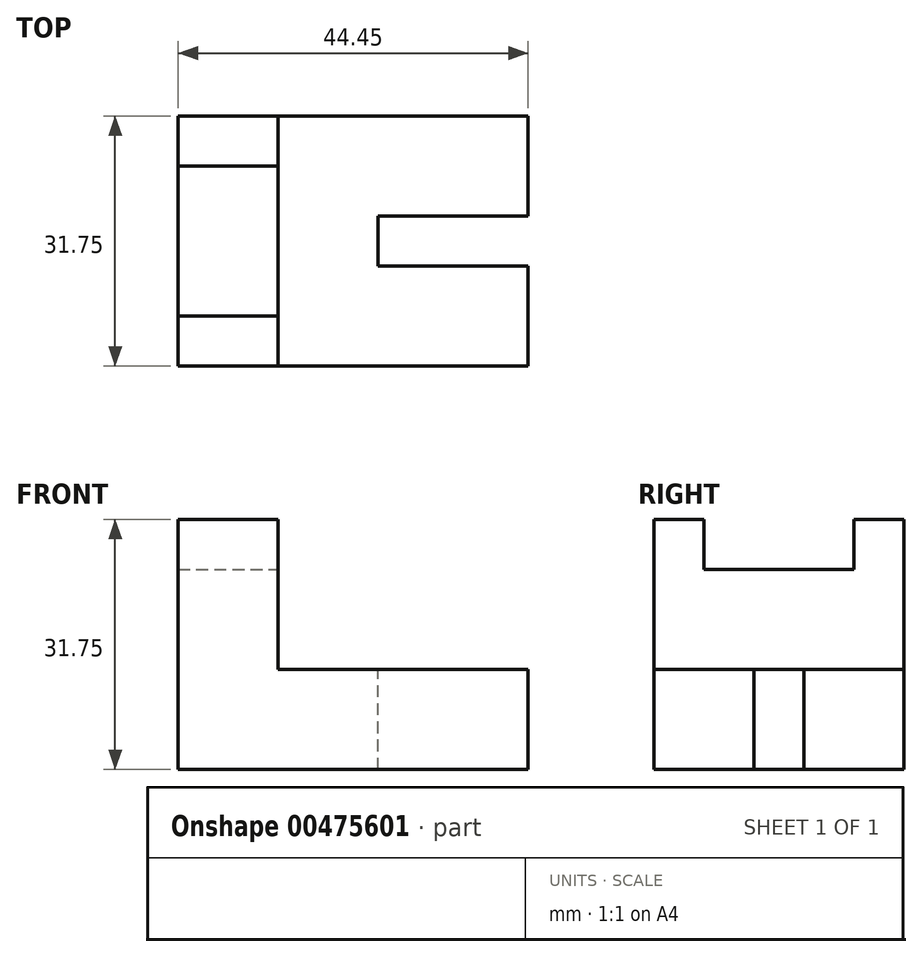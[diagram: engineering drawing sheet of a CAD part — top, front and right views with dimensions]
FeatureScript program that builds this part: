
annotation { "Feature Type Name" : "Feature", "Feature Type Description" : "" }
export const myFeature = defineFeature(function(context is Context, id is Id, definition is map)
    precondition{}
    {
        {
            var Q0;
            Q0=qCreatedBy(makeId("Front.planeOp"),FACE);
            var sketch = newSketch(context, id + "F0", { "sketchPlane" : qUnion([Q0])});
            skLineSegment(sketch, "E0", {"start": v(-27.1, 21.23) * mm, "end": v(-27.1, -10.52) * mm});
            skLineSegment(sketch, "E1", {"start": v(-27.1, -10.52) * mm, "end": v(17.35, -10.52) * mm});
            skLineSegment(sketch, "E2", {"start": v(17.35, -10.52) * mm, "end": v(17.35, 2.18) * mm});
            skLineSegment(sketch, "E3", {"start": v(-27.1, 21.23) * mm, "end": v(-14.4, 21.23) * mm});
            skLineSegment(sketch, "E4", {"start": v(-14.4, 21.23) * mm, "end": v(-14.4, 2.18) * mm});
            skLineSegment(sketch, "E5", {"start": v(-14.4, 2.18) * mm, "end": v(17.35, 2.18) * mm});
            skSolve(sketch);
        }
        {
            var Q0;
            Q0 = qSketchRegion(id + "F0", true);
            extrude(context, id + "F1", {"entities" : qUnion([Q0]), "depth" : 31.75 * mm});
        }
        {
            var Q0;
            Q0=makeQuery(id+"F1.opExtrude","SWEPT_FACE",FACE,{"disambiguationData":[OSD([sQuery(id+"F0.wireOp",EDGE,"E5")])]});
            var sketch = newSketch(context, id + "F2", { "sketchPlane" : qUnion([Q0])});
            skLineSegment(sketch, "E6", {"start": v(17.35, -12.7) * mm, "end": v(-1.7, -12.7) * mm});
            skLineSegment(sketch, "E7", {"start": v(-1.7, -12.7) * mm, "end": v(-1.7, -19.05) * mm});
            skLineSegment(sketch, "E8", {"start": v(-1.7, -19.05) * mm, "end": v(17.35, -19.05) * mm});
            skSolve(sketch);
        }
        {
            var Q0;
            Q0 = qSketchRegion(id + "F2", true);
            var Q1;
            {var subQ0=sQuery(id+"F2.wireOp",EDGE,"E6");Q1=makeQuery(id+"F2.imprint","IMPRINT",FACE,{"disambiguationData":[TD([[makeQuery(id+"F2.imprint","IMPRINT",EDGE,{"derivedFrom":subQ0}),1.0]])]});}
            extrude(context, id + "F3", {"entities" : qUnion([Q0, Q1]), "operationType" : NewBodyOperationType.REMOVE, "oppositeDirection" : true, "depth" : 12.7 * mm});
        }
        {
            var Q0;
            Q0=makeQuery(id+"F1.opExtrude","SWEPT_FACE",FACE,{"disambiguationData":[OSD([sQuery(id+"F0.wireOp",EDGE,"E4")])]});
            var sketch = newSketch(context, id + "F4", { "sketchPlane" : qUnion([Q0])});
            skLineSegment(sketch, "E9", {"start": v(-25.4, 21.23) * mm, "end": v(-25.4, 14.88) * mm});
            skLineSegment(sketch, "E10", {"start": v(-25.4, 14.88) * mm, "end": v(-6.35, 14.88) * mm});
            skLineSegment(sketch, "E11", {"start": v(-6.35, 14.88) * mm, "end": v(-6.35, 21.23) * mm});
            skSolve(sketch);
        }
        {
            var Q0;
            {var subQ0=sQuery(id+"F4.wireOp",EDGE,"E9");Q0=makeQuery(id+"F4.imprint","IMPRINT",FACE,{"disambiguationData":[TD([[makeQuery(id+"F4.imprint","IMPRINT",EDGE,{"derivedFrom":subQ0}),1.0]])]});}
            extrude(context, id + "F5", {"entities" : qUnion([Q0]), "operationType" : NewBodyOperationType.REMOVE, "oppositeDirection" : true, "depth" : 12.7 * mm});
        }
    });
